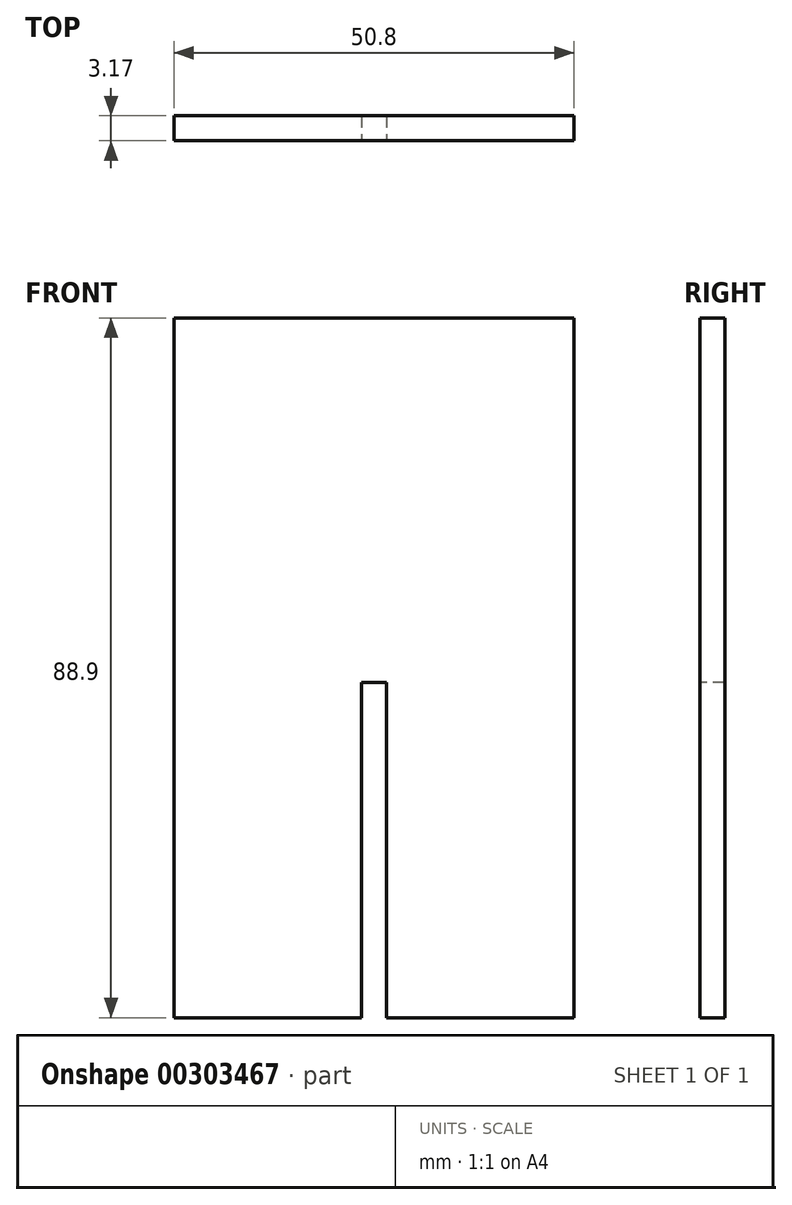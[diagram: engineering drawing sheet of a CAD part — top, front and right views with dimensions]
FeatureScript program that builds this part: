
annotation { "Feature Type Name" : "Feature", "Feature Type Description" : "" }
export const myFeature = defineFeature(function(context is Context, id is Id, definition is map)
    precondition{}
    {
        {
            var Q0;
            Q0=qCreatedBy(makeId("Front.planeOp"),FACE);
            var sketch = newSketch(context, id + "F0", { "sketchPlane" : qUnion([Q0])});
            skLineSegment(sketch, "E0.bottom", {"start": v(-25.4, 44.45) * mm, "end": v(25.4, 44.45) * mm});
            skLineSegment(sketch, "E0.top", {"start": v(-25.4, -44.45) * mm, "end": v(25.4, -44.45) * mm});
            skLineSegment(sketch, "E0.left", {"start": v(-25.4, 44.45) * mm, "end": v(-25.4, -44.45) * mm});
            skLineSegment(sketch, "E0.right", {"start": v(25.4, 44.45) * mm, "end": v(25.4, -44.45) * mm});
            skPoint(sketch, "E0.middle", {"position": v(0, 0) * mm});
            skSolve(sketch);
        }
        {
            var Q0;
            Q0=qSketchRegion(id+"F0",true);
            extrude(context, id + "F1", {"entities" : qUnion([Q0]), "depth" : 3.17 * mm});
        }
        {
            var Q0;
            Q0=makeQuery(id+"F1.opExtrude","CAP_FACE",FACE,{"disambiguationData":[OSD([sQuery(id+"F0.wireOp",EDGE,"E0.bottom"),sQuery(id+"F0.wireOp",EDGE,"E0.top"),sQuery(id+"F0.wireOp",EDGE,"E0.left"),sQuery(id+"F0.wireOp",EDGE,"E0.right")])],"isStart":false});
            var sketch = newSketch(context, id + "F2", { "sketchPlane" : qUnion([Q0])});
            skLineSegment(sketch, "E1.bottom", {"start": v(1.59, -1.88) * mm, "end": v(-1.59, -1.88) * mm});
            skLineSegment(sketch, "E1.top", {"start": v(1.59, -44.74) * mm, "end": v(-1.59, -44.74) * mm});
            skLineSegment(sketch, "E1.left", {"start": v(1.59, -1.88) * mm, "end": v(1.59, -44.74) * mm});
            skLineSegment(sketch, "E1.right", {"start": v(-1.59, -1.88) * mm, "end": v(-1.59, -44.74) * mm});
            skPoint(sketch, "E1.middle", {"position": v(0, -23.3) * mm});
            skSolve(sketch);
        }
        {
            var Q0;
            Q0=qSketchRegion(id+"F2",true);
            extrude(context, id + "F3", {"entities" : qUnion([Q0]), "operationType" : NewBodyOperationType.REMOVE, "oppositeDirection" : true, "depth" : 3.17 * mm});
        }
        {
            var Q0;
            Q0=qSketchRegion(id+"F2",true);
            extrude(context, id + "F4", {"entities" : qUnion([Q0]), "operationType" : NewBodyOperationType.REMOVE, "oppositeDirection" : true, "depth" : 3.17 * mm});
        }
    });
